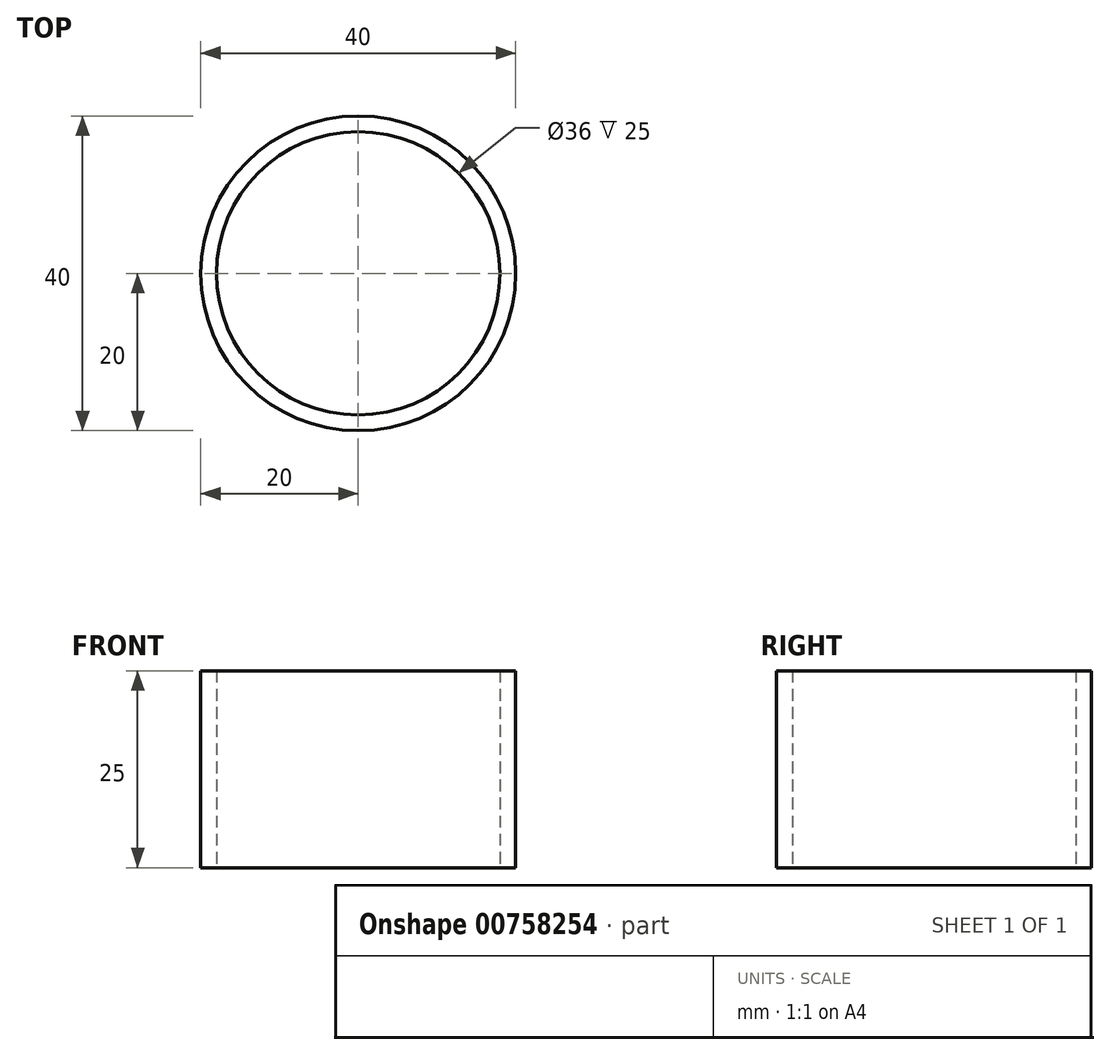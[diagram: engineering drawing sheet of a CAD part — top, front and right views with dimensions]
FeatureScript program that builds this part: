
annotation { "Feature Type Name" : "Feature", "Feature Type Description" : "" }
export const myFeature = defineFeature(function(context is Context, id is Id, definition is map)
    precondition{}
    {
        {
            var Q0;
            Q0=qCreatedBy(makeId("Top.planeOp"),FACE);
            var sketch = newSketch(context, id + "F0", { "sketchPlane" : qUnion([Q0])});
            skCircle(sketch, "E0", {"center": v(0, 0) * mm, "radius": 20 * mm});
            skCircle(sketch, "E1", {"center": v(0, 0) * mm, "radius": 18 * mm});
            skSolve(sketch);
        }
        {
            var Q0;
            Q0=makeQuery(id+"F0.imprint","IMPRINT",FACE,{"disambiguationData":[TD([[makeQuery(id+"F0.imprint","IMPRINT",EDGE,{"derivedFrom":sQuery(id+"F0.wireOp",EDGE,"E0")}),1.0]])]});
            extrude(context, id + "F1", {"entities" : qUnion([Q0]), "depth" : 25 * mm, "offsetDistance" : 25 * mm});
        }
    });
